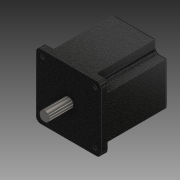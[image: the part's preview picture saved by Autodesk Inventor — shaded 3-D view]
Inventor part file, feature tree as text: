
AUTODESK INVENTOR PART (.ipt)
format: ipt  version: 2020 (Build 240168000, 168)  size: 305,664 bytes
history: native  units: mm
features: extrude x3, sketch x3, fillet x1
ambient origin geometry x8: Origin, YZ Plane, XZ Plane, XY Plane, X Axis, Y Axis, Z Axis, Center Point
bodies: Solid1 (feature_tree)
feature tree (7):
  extrude  "Extrusion1"  Depth=6.0mm
  extrude  "Extrusion2"  Depth=69.596mm
  fillet  "Fillet1"  Radius=69.596mm
  extrude  "Extrusion3"  Depth=31.75mm
  sketch  "Sketch1"  dims[d0=85.852mm d1=6.0mm]
  sketch  "Sketch2"  dims[d5=5.5118mm d6=69.596mm d7=69.596mm]
  sketch  "Sketch3"  dims[d8=69.596mm d9=69.596mm d10=34.798mm d11=34.798mm d12=8.382mm d13=0.0mm d14=56.0mm d15=36.0mm d16=56.0mm d17=36.0mm d18=5.0mm d19=80.01mm d20=0.0mm d21=3.0mm d22=12.7mm d23=31.75mm d24=0.0mm d30=28.0mm d31=28.0mm]
